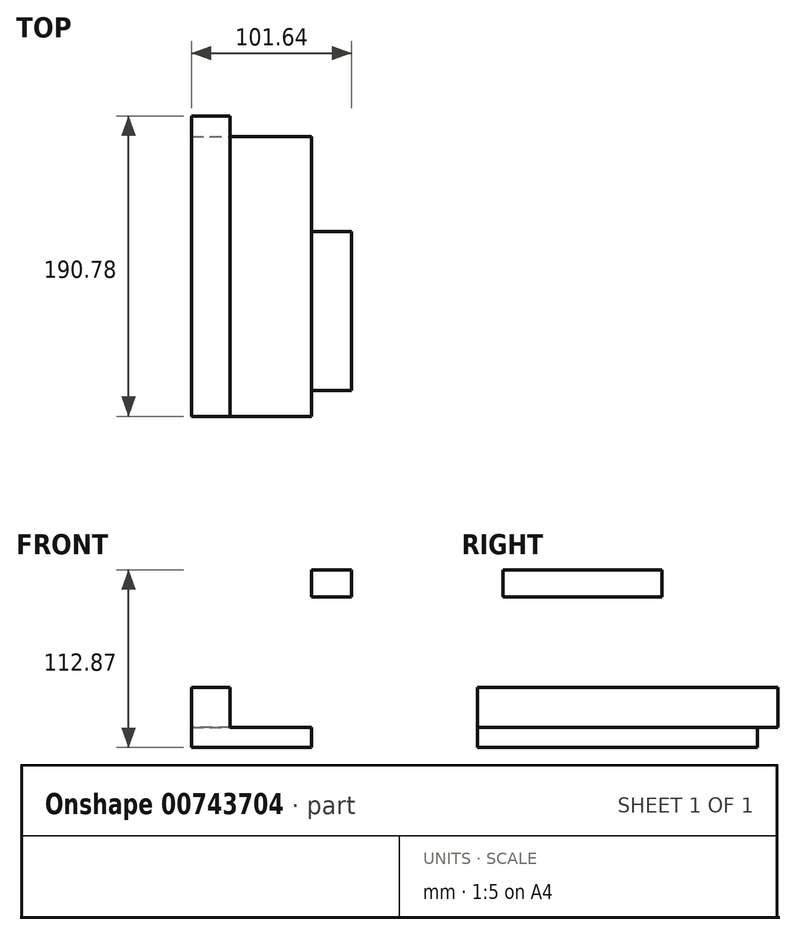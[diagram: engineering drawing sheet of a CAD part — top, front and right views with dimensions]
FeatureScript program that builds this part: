
annotation { "Feature Type Name" : "Feature", "Feature Type Description" : "" }
export const myFeature = defineFeature(function(context is Context, id is Id, definition is map)
    precondition{}
    {
        {
            var Q0;
            Q0=qCreatedBy(makeId("Top.planeOp"),FACE);
            var sketch = newSketch(context, id + "F0", { "sketchPlane" : qUnion([Q0])});
            skLineSegment(sketch, "E0.bottom", {"start": v(-43.54, 85.68) * mm, "end": v(32.66, 85.68) * mm});
            skLineSegment(sketch, "E0.top", {"start": v(-43.54, -92.12) * mm, "end": v(32.66, -92.12) * mm});
            skLineSegment(sketch, "E0.left", {"start": v(-43.54, 85.68) * mm, "end": v(-43.54, -92.12) * mm});
            skLineSegment(sketch, "E0.right", {"start": v(32.66, 85.68) * mm, "end": v(32.66, -92.12) * mm});
            skSolve(sketch);
        }
        {
            var Q0;
            Q0=makeQuery(id+"F0.imprint","IMPRINT",FACE,{"disambiguationData":[TD([[makeQuery(id+"F0.imprint","IMPRINT",EDGE,{"derivedFrom":sQuery(id+"F0.wireOp",EDGE,"E0.bottom")}),-1.0]])]});
            extrude(context, id + "F1", {"entities" : qUnion([Q0]), "depth" : 12.7 * mm, "offsetDistance" : 25.4 * mm});
        }
        {
            var Q0;
            Q0=makeQuery(id+"F1.opExtrude","CAP_FACE",FACE,{"disambiguationData":[OSD([sQuery(id+"F0.wireOp",EDGE,"E0.bottom"),sQuery(id+"F0.wireOp",EDGE,"E0.top"),sQuery(id+"F0.wireOp",EDGE,"E0.left"),sQuery(id+"F0.wireOp",EDGE,"E0.right")])],"isStart":false});
            var sketch = newSketch(context, id + "F2", { "sketchPlane" : qUnion([Q0])});
            skLineSegment(sketch, "E1.bottom", {"start": v(-19.08, -92.12) * mm, "end": v(-43.58, -92.12) * mm});
            skLineSegment(sketch, "E1.top", {"start": v(-19.08, 98.66) * mm, "end": v(-43.58, 98.66) * mm});
            skLineSegment(sketch, "E1.left", {"start": v(-19.08, -92.12) * mm, "end": v(-19.08, 98.66) * mm});
            skLineSegment(sketch, "E1.right", {"start": v(-43.58, -92.12) * mm, "end": v(-43.58, 98.66) * mm});
            skPoint(sketch, "E1.middle", {"position": v(-31.33, 3.27) * mm});
            skLineSegment(sketch, "E2.bottom", {"start": v(-19.08, 42.85) * mm, "end": v(-19.08, 42.85) * mm});
            skLineSegment(sketch, "E2.top", {"start": v(-19.08, 96.16) * mm, "end": v(-19.08, 96.16) * mm});
            skLineSegment(sketch, "E2.left", {"start": v(-19.08, 42.85) * mm, "end": v(-19.08, 96.16) * mm});
            skLineSegment(sketch, "E2.right", {"start": v(-19.08, 42.85) * mm, "end": v(-19.08, 96.16) * mm});
            skPoint(sketch, "E2.middle", {"position": v(-19.08, 69.5) * mm});
            skSolve(sketch);
        }
        {
            var Q0;
            {var subQ0=makeQuery(id+"F1.opExtrude","CAP_EDGE",EDGE,{"disambiguationData":[OSD([sQuery(id+"F0.wireOp",EDGE,"E0.left")])],"isStart":false});Q0=makeQuery(id+"F2.imprint","IMPRINT",FACE,{"disambiguationData":[TD([[makeQuery(id+"F2.imprint","IMPRINT",EDGE,{"derivedFrom":subQ0}),1.0]])]});}
            var Q1;
            Q1 = qSketchRegion(id + "F2", true);
            extrude(context, id + "F3", {"entities" : qUnion([Q0, Q1]), "operationType" : NewBodyOperationType.ADD, "depth" : 25.4 * mm, "offsetDistance" : 25.4 * mm});
        }
        {
            var Q0;
            Q0=makeQuery(id+"F1.opExtrude","SWEPT_FACE",FACE,{"disambiguationData":[OSD([sQuery(id+"F0.wireOp",EDGE,"E0.right")])]});
            var sketch = newSketch(context, id + "F4", { "sketchPlane" : qUnion([Q0])});
            skLineSegment(sketch, "E3.bottom", {"start": v(25.16, 107.44) * mm, "end": v(-75.8, 107.44) * mm});
            skLineSegment(sketch, "E3.top", {"start": v(25.16, 95.67) * mm, "end": v(-75.8, 95.67) * mm});
            skLineSegment(sketch, "E3.left", {"start": v(25.16, 107.44) * mm, "end": v(25.16, 95.67) * mm});
            skLineSegment(sketch, "E3.right", {"start": v(-75.8, 107.44) * mm, "end": v(-75.8, 95.67) * mm});
            skPoint(sketch, "E3.middle", {"position": v(-25.32, 101.56) * mm});
            skSolve(sketch);
        }
        {
            var Q0;
            Q0 = qSketchRegion(id + "F4", true);
            extrude(context, id + "F5", {"entities" : qUnion([Q0]), "depth" : 25.4 * mm, "offsetDistance" : 25.4 * mm});
        }
        {
            var Q0;
            Q0=makeQuery(id+"F5.opExtrude","SWEPT_FACE",FACE,{"disambiguationData":[OSD([sQuery(id+"F4.wireOp",EDGE,"E3.bottom")])]});
            var sketch = newSketch(context, id + "F6", { "sketchPlane" : qUnion([Q0])});
            skSolve(sketch);
        }
        {
            var Q0;
            {var subQ0=sQuery(id+"F4.wireOp",EDGE,"E3.bottom");Q0=makeQuery(id+"F6.imprint","IMPRINT",FACE,{"disambiguationData":[TD([[makeQuery(id+"F6.imprint","IMPRINT",EDGE,{"derivedFrom":makeQuery(id+"F5.opExtrude","CAP_EDGE",EDGE,{"disambiguationData":[OSD([subQ0])],"isStart":true})}),1.0]])]});}
            extrude(context, id + "F7", {"entities" : qUnion([Q0]), "operationType" : NewBodyOperationType.ADD, "depth" : 5.43 * mm, "offsetDistance" : 25.4 * mm});
        }
    });
